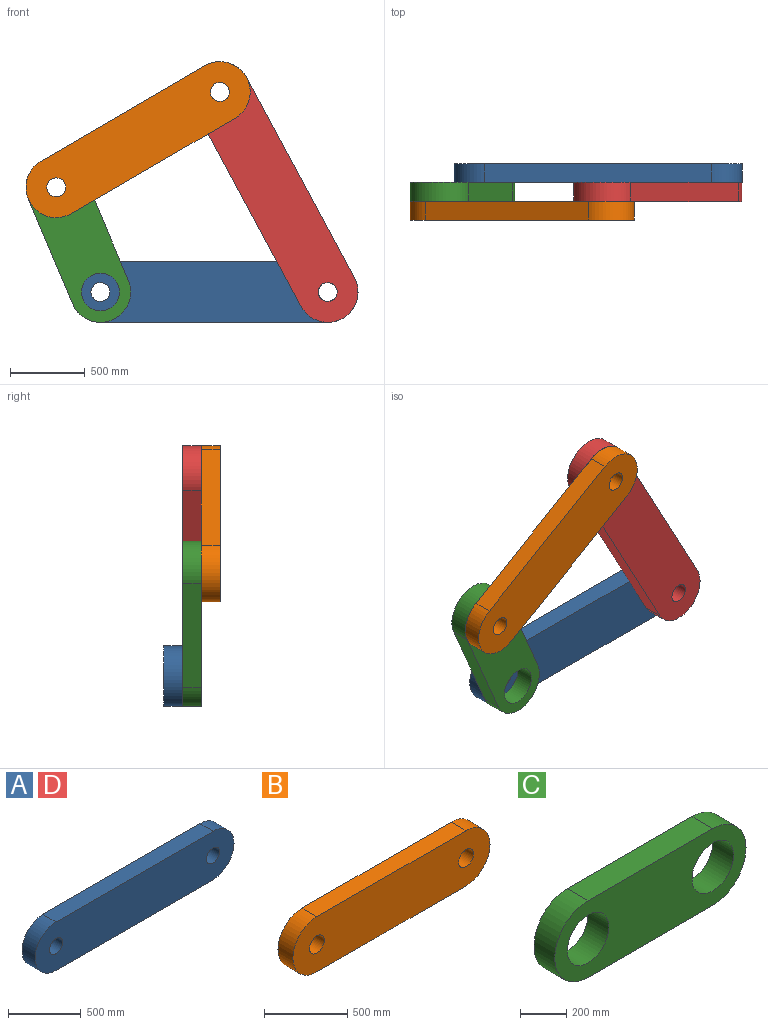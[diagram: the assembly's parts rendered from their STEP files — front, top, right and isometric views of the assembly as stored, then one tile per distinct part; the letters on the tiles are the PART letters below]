
ASSEMBLY  parts=4 mates=7
PART A: 8 faces, bbox 1930.4x127x406.4 mm
  f0: cylinder r=203.2mm len=406.4mm, axis (0,1,0), area 81073.2mm2, adj f1,f5,f6,f7
  f1: plane 1524x127mm, normal (0,0,-1), area 193548mm2, adj f0,f2,f6,f7
  f2: cylinder r=203.2mm len=406.4mm, axis (0,1,0), area 81073.2mm2, adj f1,f5,f6,f7
  f3: cylinder r=63.5mm len=127mm, axis (0,1,0), area 50670.7mm2, adj f6,f7
  f4: cylinder r=63.5mm len=127mm, axis (0,1,0), area 50670.7mm2, adj f6,f7
  f5: plane 1524x127mm, normal (0,0,1), area 193548mm2, adj f0,f2,f6,f7
  f6: plane 1930.4x406.4mm, normal (0,-1,0), area 723735.3mm2, adj f0,f1,f2,f3,f4,f5
  f7: plane 1930.4x406.4mm, normal (0,1,0), area 723735.3mm2, adj f0,f1,f2,f3,f4,f5
PART B: 8 faces, bbox 1676.4x127x406.4 mm
  f0: cylinder r=203.2mm len=406.4mm, axis (0,1,0), area 81073.2mm2, adj f1,f5,f6,f7
  f1: plane 1270x127mm, normal (0,0,-1), area 161290mm2, adj f0,f2,f6,f7
  f2: cylinder r=203.2mm len=406.4mm, axis (0,1,0), area 81073.2mm2, adj f1,f5,f6,f7
  f3: cylinder r=63.5mm len=127mm, axis (0,1,0), area 50670.7mm2, adj f6,f7
  f4: cylinder r=63.5mm len=127mm, axis (0,1,0), area 50670.7mm2, adj f6,f7
  f5: plane 1270x127mm, normal (0,0,1), area 161290mm2, adj f0,f2,f6,f7
  f6: plane 1676.4x406.4mm, normal (0,-1,0), area 620509.7mm2, adj f0,f1,f2,f3,f4,f5
  f7: plane 1676.4x406.4mm, normal (0,1,0), area 620509.7mm2, adj f0,f1,f2,f3,f4,f5
PART C: 8 faces, bbox 1168.4x127x406.4 mm
  f0: cylinder r=203.2mm len=406.4mm, axis (0,1,0), area 81073.2mm2, adj f1,f5,f6,f7
  f1: plane 762x127mm, normal (0,0,-1), area 96774mm2, adj f0,f2,f6,f7
  f2: cylinder r=203.2mm len=406.4mm, axis (0,1,0), area 81073.2mm2, adj f1,f5,f6,f7
  f3: cylinder r=127mm len=254mm, axis (0,1,0), area 101341.5mm2, adj f6,f7
  f4: cylinder r=127mm len=254mm, axis (0,1,0), area 101341.5mm2, adj f6,f7
  f5: plane 762x127mm, normal (0,0,1), area 96774mm2, adj f0,f2,f6,f7
  f6: plane 1168.4x406.4mm, normal (0,-1,0), area 338052.4mm2, adj f0,f1,f2,f3,f4,f5
  f7: plane 1168.4x406.4mm, normal (0,1,0), area 338052.4mm2, adj f0,f1,f2,f3,f4,f5
PART D: same geometry as A
PLACE A t=(11.47,85.07,22.43)mm fixed
PLACE B rot(axis=(0,-1,0),30.2deg) t=(-498.08,-168.93,1044.29)mm
PLACE C rot(axis=(0,1,0),67.1deg) t=(-898.61,-41.93,373.48)mm
PLACE D rot(axis=(0,1,0),61.7deg) t=(412,-41.93,693.24)mm
MATE planar A.f6 <-> D.f7  axis (0,-1,0) through (11.47,-41.93,22.43)mm
MATE planar C.f6 <-> B.f7  axis (0,-1,0) through (-898.61,-168.93,373.48)mm
MATE cylindrical A.f0 <-> C.f2  axis (0,1,0) through (-750.53,-41.93,22.43)mm
MATE planar A.f6 <-> C.f7  axis (0,-1,0) through (11.47,-41.93,22.43)mm
MATE cylindrical D.f2 <-> A.f2  axis (0,-1,0) through (773.47,-168.93,22.43)mm
MATE cylindrical B.f2 <-> D.f0  axis (0,-1,0) through (50.54,-295.93,1364.05)mm
MATE cylindrical B.f0 <-> C.f0  axis (0,-1,0) through (-1046.69,-295.93,724.52)mm
